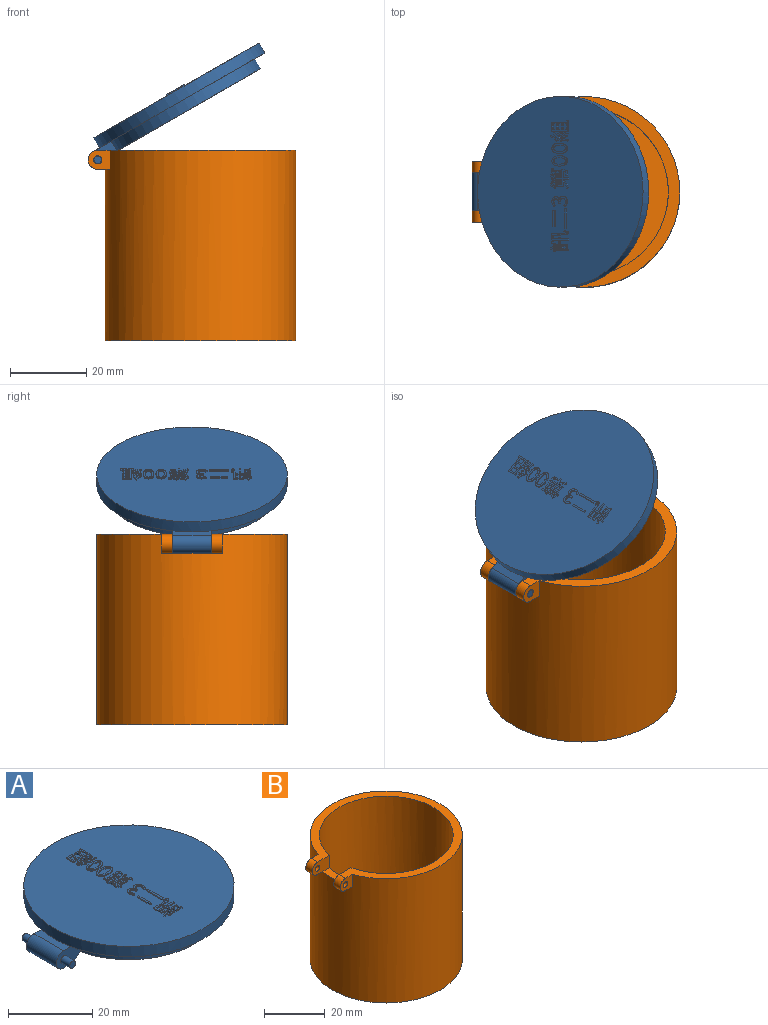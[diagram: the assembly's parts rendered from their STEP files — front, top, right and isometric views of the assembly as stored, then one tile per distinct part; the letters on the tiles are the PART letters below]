
ASSEMBLY  parts=2 mates=1
PART A: 240 faces, bbox 54.4x50x8.3 mm
  f0: plane 50x50mm, normal (0,0,1), area 1893.5mm2, adj f5,f15,f16,f17,f18,f20,f21,f22
  f1: plane 10x2.43mm, normal (0,0,1), area 20.9mm2, adj f2,f3,f5,f13
  f2: plane 8x5mm, normal (0,-1,0), area 31.8mm2, adj f1,f4,f6,f7,f9,f13,f14
  f3: plane 8x5mm, normal (0,1,0), area 31.8mm2, adj f1,f4,f6,f7,f11,f13,f14
  f4: plane 10x1.5mm, normal (0,0,-1), area 15mm2, adj f2,f3,f13,f14
  f5: cylinder r=25mm len=50mm, axis (0,0,1), area 471.2mm2, adj f0,f1,f6
  f6: plane 50x49.5mm, normal (0,0,-1), area 412.7mm2, adj f2,f3,f5,f7
  f7: cylinder r=22mm len=44mm, axis (0,0,1), area 384.4mm2, adj f2,f3,f6,f8
  f8: plane 44x43.42mm, normal (0,0,-1), area 1516.7mm2, adj f7,f14
  f9: cylinder r=1mm len=3mm, axis (0,1,0), area 18.8mm2, adj f2,f10
  f10: plane 2x2mm, normal (0,-1,0), area 3.1mm2, adj f9
  f11: cylinder r=1mm len=3mm, axis (0,-1,0), area 18.8mm2, adj f3,f12
  f12: plane 2x2mm, normal (0,1,0), area 3.1mm2, adj f11
  f13: cylinder r=2.5mm len=10mm, axis (0,-1,0), area 78.5mm2, adj f1,f2,f3,f4
  f14: cylinder r=5mm len=10mm, axis (0,1,0), area 46.4mm2, adj f2,f3,f4,f8
  f15: plane 0.33x0.3mm, normal (0.85,0.53,0), area 0.1mm2, adj f0,f16,f18,f19
  f16: extruded ~0.76x0.43mm, area 0.3mm2, adj f0,f15,f17,f19
  f17: plane 0.31x0.3mm, normal (-0.87,-0.49,0), area 0.1mm2, adj f0,f16,f18,f19
  f18: extruded ~0.79x0.42mm, area 0.3mm2, adj f0,f15,f17,f19
  f19: plane 0.97x0.74mm, normal (0,0,1), area 0.3mm2, adj f15,f16,f17,f18
  f20: plane 0.36x0.3mm, normal (0,1,0), area 0.1mm2, adj f0,f21,f23,f24
  f21: plane 2.13x0.3mm, normal (-1,0,0), area 0.6mm2, adj f0,f20,f22,f24
  f22: plane 0.36x0.3mm, normal (0,-1,0), area 0.1mm2, adj f0,f21,f23,f24
  f23: plane 2.13x0.3mm, normal (1,0,0), area 0.6mm2, adj f0,f20,f22,f24
  f24: plane 2.13x0.36mm, normal (0,0,1), area 0.8mm2, adj f20,f21,f22,f23
  f25: plane 1.67x0.3mm, normal (1,0,0), area 0.5mm2, adj f0,f26,f28,f29
  f26: plane 0.35x0.3mm, normal (0,1,0), area 0.1mm2, adj f0,f25,f27,f29
  f27: plane 1.67x0.3mm, normal (-1,0,0), area 0.5mm2, adj f0,f26,f28,f29
  f28: plane 0.35x0.3mm, normal (0,-1,0), area 0.1mm2, adj f0,f25,f27,f29
  f29: plane 1.67x0.35mm, normal (0,0,1), area 0.6mm2, adj f25,f26,f27,f28
  f30: plane 0.96x0.3mm, normal (1,0,0), area 0.3mm2, adj f31,f39,f40,f41
  f31: plane 0.98x0.3mm, normal (0,-1,0), area 0.3mm2, adj f30,f32,f40,f41
  f32: plane 0.96x0.3mm, normal (-1,0,0), area 0.3mm2, adj f31,f39,f40,f41
  f33: plane 1.71x0.3mm, normal (0,1,0), area 0.5mm2, adj f0,f34,f38,f40
  f34: plane 1.68x0.3mm, normal (-1,0,0), area 0.5mm2, adj f0,f33,f35,f40
  f35: plane 1.99x0.3mm, normal (0,-1,0), area 0.6mm2, adj f0,f34,f36,f40
  f36: plane 0.36x0.3mm, normal (1,0,0), area 0.1mm2, adj f0,f35,f37,f40
  f37: plane 0.3x0.28mm, normal (0,1,0), area 0.1mm2, adj f0,f36,f38,f40
  f38: plane 1.32x0.3mm, normal (1,0,0), area 0.4mm2, adj f0,f33,f37,f40
  f39: plane 0.98x0.3mm, normal (0,1,0), area 0.3mm2, adj f30,f32,f40,f41
  f40: plane 1.99x1.68mm, normal (0,0,1), area 2mm2, adj f30,f31,f32,f33,f34,f35,f36,f37
  f41: plane 0.98x0.96mm, normal (0,0,1), area 0.9mm2, adj f30,f31,f32,f39
  f42: plane 0.35x0.3mm, normal (0,-1,0), area 0.1mm2, adj f0,f43,f45,f46
  f43: plane 1.68x0.3mm, normal (1,0,0), area 0.5mm2, adj f0,f42,f44,f46
  f44: plane 0.35x0.3mm, normal (0,1,0), area 0.1mm2, adj f0,f43,f45,f46
  f45: plane 1.68x0.3mm, normal (-1,0,0), area 0.5mm2, adj f0,f42,f44,f46
  f46: plane 1.68x0.35mm, normal (0,0,1), area 0.6mm2, adj f42,f43,f44,f45
  f47: plane 2.58x0.3mm, normal (-1,0,0), area 0.8mm2, adj f0,f48,f66,f67
  f48: plane 0.42x0.3mm, normal (0,-1,0), area 0.1mm2, adj f0,f47,f49,f67
  f49: plane 0.74x0.3mm, normal (1,0,0), area 0.2mm2, adj f0,f48,f50,f67
  f50: plane 1.75x0.3mm, normal (0,-1,0), area 0.5mm2, adj f0,f49,f51,f67
  f51: plane 0.8x0.3mm, normal (-1,0,0), area 0.2mm2, adj f0,f50,f52,f67
  f52: plane 0.41x0.3mm, normal (0,-1,0), area 0.1mm2, adj f0,f51,f53,f67
  f53: plane 0.8x0.3mm, normal (1,0,0), area 0.2mm2, adj f0,f52,f54,f67
  f54: plane 2.5x0.3mm, normal (0,-1,0), area 0.7mm2, adj f0,f53,f55,f67
  f55: plane 0.42x0.3mm, normal (1,0,0), area 0.1mm2, adj f0,f54,f56,f67
  f56: plane 2.5x0.3mm, normal (0,1,0), area 0.7mm2, adj f0,f55,f57,f67
  f57: plane 0.78x0.3mm, normal (1,0,0), area 0.2mm2, adj f0,f56,f58,f67
  f58: plane 0.41x0.3mm, normal (0,1,0), area 0.1mm2, adj f0,f57,f59,f67
  f59: plane 0.78x0.3mm, normal (-1,0,0), area 0.2mm2, adj f0,f58,f60,f67
  f60: plane 1.75x0.3mm, normal (0,1,0), area 0.5mm2, adj f0,f59,f61,f67
  f61: plane 0.98x0.3mm, normal (1,0,0), area 0.3mm2, adj f0,f60,f62,f67
  f62: extruded ~4.55x0.56mm, area 1.4mm2, adj f0,f61,f63,f67
  f63: extruded ~0.94x0.53mm, area 0.4mm2, adj f0,f62,f64,f67
  f64: extruded ~0.32x0.3mm, area 0.1mm2, adj f0,f63,f65,f67
  f65: extruded ~0.8x0.3mm, area 0.2mm2, adj f0,f64,f66,f67
  f66: extruded ~4.54x0.3mm, area 1.4mm2, adj f0,f47,f65,f67
  f67: plane 5.08x3.29mm, normal (0,0,1), area 5.9mm2, adj f47,f48,f49,f50,f51,f52,f53,f54
  f68: plane 4.23x0.3mm, normal (-1,0,0), area 1.3mm2, adj f0,f69,f71,f72
  f69: plane 0.47x0.3mm, normal (0,-1,0), area 0.1mm2, adj f0,f68,f70,f72
  f70: plane 4.23x0.3mm, normal (1,0,0), area 1.3mm2, adj f0,f69,f71,f72
  f71: plane 0.47x0.3mm, normal (0,1,0), area 0.1mm2, adj f0,f68,f70,f72
  f72: plane 4.23x0.47mm, normal (0,0,1), area 2mm2, adj f68,f69,f70,f71
  f73: plane 5.23x0.3mm, normal (-1,0,0), area 1.6mm2, adj f0,f74,f76,f77
  f74: plane 0.48x0.3mm, normal (0,-1,0), area 0.1mm2, adj f0,f73,f75,f77
  f75: plane 5.23x0.3mm, normal (1,0,0), area 1.6mm2, adj f0,f74,f76,f77
  f76: plane 0.48x0.3mm, normal (0,1,0), area 0.1mm2, adj f0,f73,f75,f77
  f77: plane 5.23x0.48mm, normal (0,0,1), area 2.5mm2, adj f73,f74,f75,f76
  f78: extruded ~1.39x0.59mm, area 0.5mm2, adj f0,f79,f93,f94
  f79: extruded ~1.39x1.24mm, area 0.6mm2, adj f0,f78,f80,f94
  f80: extruded ~1.1x0.93mm, area 0.5mm2, adj f0,f79,f81,f94
  f81: plane 0.3x0.02mm, normal (0,1,0), area 0mm2, adj f0,f80,f82,f94
  f82: extruded ~1.05x0.78mm, area 0.4mm2, adj f0,f81,f83,f94
  f83: extruded ~1.26x1.09mm, area 0.6mm2, adj f0,f82,f84,f94
  f84: extruded ~1.22x0.52mm, area 0.4mm2, adj f0,f83,f85,f94
  f85: plane 0.35x0.3mm, normal (0.65,-0.76,0), area 0.1mm2, adj f0,f84,f86,f94
  f86: extruded ~0.9x0.43mm, area 0.3mm2, adj f0,f85,f87,f94
  f87: extruded ~0.74x0.7mm, area 0.3mm2, adj f0,f86,f88,f94
  f88: extruded ~1.2x0.83mm, area 0.5mm2, adj f0,f87,f89,f94
  f89: plane 0.42x0.3mm, normal (0,-1,0), area 0.1mm2, adj f0,f88,f90,f94
  f90: extruded ~1.35x0.87mm, area 0.5mm2, adj f0,f89,f91,f94
  f91: extruded ~0.88x0.81mm, area 0.4mm2, adj f0,f90,f92,f94
  f92: extruded ~1.08x0.5mm, area 0.4mm2, adj f0,f91,f93,f94
  f93: plane 0.36x0.3mm, normal (-0.61,-0.79,0), area 0.1mm2, adj f0,f78,f92,f94
  f94: plane 4.51x2.79mm, normal (0,0,1), area 4.4mm2, adj f78,f79,f80,f81,f82,f83,f84,f85
  f95: plane 0.51x0.3mm, normal (1,0,0), area 0.2mm2, adj f0,f96,f107,f108
  f96: plane 0.3x0.23mm, normal (-0.8,-0.61,0), area 0.1mm2, adj f0,f95,f97,f108
  f97: extruded ~0.6x0.56mm, area 0.2mm2, adj f0,f96,f98,f108
  f98: plane 0.3x0.29mm, normal (0.77,0.64,0), area 0.1mm2, adj f0,f97,f99,f108
  f99: extruded ~0.53x0.53mm, area 0.2mm2, adj f0,f98,f100,f108
  f100: plane 1.12x0.3mm, normal (1,0,0), area 0.3mm2, adj f0,f99,f101,f108
  f101: plane 0.36x0.3mm, normal (0,1,0), area 0.1mm2, adj f0,f100,f102,f108
  f102: plane 1.52x0.3mm, normal (-1,0,0), area 0.5mm2, adj f0,f101,f103,f108
  f103: extruded ~0.36x0.3mm, area 0.1mm2, adj f0,f102,f104,f108
  f104: plane 0.39x0.3mm, normal (-0.96,0.27,0), area 0.1mm2, adj f0,f103,f105,f108
  f105: extruded ~1.29x0.9mm, area 0.5mm2, adj f0,f104,f106,f108
  f106: extruded ~0.31x0.3mm, area 0.1mm2, adj f0,f105,f107,f108
  f107: extruded ~0.77x0.61mm, area 0.3mm2, adj f0,f95,f106,f108
  f108: plane 2.64x1.6mm, normal (0,0,1), area 1.5mm2, adj f95,f96,f97,f98,f99,f100,f101,f102
  f109: plane 1.33x0.3mm, normal (1,0,0), area 0.4mm2, adj f110,f142,f143,f145
  f110: plane 0.55x0.3mm, normal (0,-1,0), area 0.2mm2, adj f109,f111,f143,f145
  f111: plane 1.42x0.3mm, normal (-1,0,0), area 0.4mm2, adj f110,f142,f143,f145
  f112: plane 0.55x0.3mm, normal (0,1,0), area 0.2mm2, adj f113,f140,f143,f144
  f113: plane 1.55x0.3mm, normal (1,0,0), area 0.5mm2, adj f112,f114,f143,f144
  f114: plane 0.55x0.3mm, normal (0,-1,0), area 0.2mm2, adj f113,f140,f143,f144
  f115: plane 2.18x0.3mm, normal (-1,0,0), area 0.7mm2, adj f0,f116,f141,f143
  f116: plane 0.55x0.3mm, normal (0,1,0), area 0.2mm2, adj f0,f115,f117,f143
  f117: plane 1.99x0.3mm, normal (1,0,0), area 0.6mm2, adj f0,f116,f118,f143
  f118: plane 1.29x0.3mm, normal (0,1,0), area 0.4mm2, adj f0,f117,f119,f143
  f119: plane 4.34x0.3mm, normal (-1,0,0), area 1.3mm2, adj f0,f118,f120,f143
  f120: plane 0.37x0.3mm, normal (0,-1,0), area 0.1mm2, adj f0,f119,f121,f143
  f121: plane 1.92x0.3mm, normal (1,0,0), area 0.6mm2, adj f0,f120,f122,f143
  f122: plane 0.55x0.3mm, normal (0,-1,0), area 0.2mm2, adj f0,f121,f123,f143
  f123: plane 1.71x0.3mm, normal (-1,0,0), area 0.5mm2, adj f0,f122,f124,f143
  f124: extruded ~1.31x0.3mm, area 0.4mm2, adj f0,f123,f125,f143
  f125: plane 1.57x0.3mm, normal (1,0,0), area 0.5mm2, adj f0,f124,f126,f143
  f126: extruded ~1.93x1.19mm, area 0.7mm2, adj f0,f125,f127,f143
  f127: extruded ~0.35x0.3mm, area 0.1mm2, adj f0,f126,f128,f143
  f128: extruded ~1.99x1.37mm, area 0.7mm2, adj f0,f127,f129,f143
  f129: plane 1.36x0.3mm, normal (0,-1,0), area 0.4mm2, adj f0,f128,f130,f143
  f130: plane 0.43x0.3mm, normal (1,0,0), area 0.1mm2, adj f0,f129,f131,f143
  f131: plane 1.53x0.3mm, normal (0,1,0), area 0.5mm2, adj f0,f130,f132,f143
  f132: plane 1.71x0.3mm, normal (1,0,0), area 0.5mm2, adj f0,f131,f133,f143
  f133: extruded ~0.85x0.3mm, area 0.3mm2, adj f0,f132,f134,f143
  f134: extruded ~0.3x0.21mm, area 0.1mm2, adj f0,f133,f135,f143
  f135: extruded ~0.67x0.3mm, area 0.2mm2, adj f0,f134,f136,f143
  f136: extruded ~0.41x0.3mm, area 0.1mm2, adj f0,f135,f137,f143
  f137: extruded ~0.75x0.3mm, area 0.2mm2, adj f0,f136,f138,f143
  f138: extruded ~0.37x0.3mm, area 0.1mm2, adj f0,f137,f139,f143
  f139: extruded ~1.32x0.31mm, area 0.4mm2, adj f0,f138,f141,f143
  f140: plane 1.55x0.3mm, normal (-1,0,0), area 0.5mm2, adj f112,f114,f143,f144
  f141: extruded ~0.3x0.18mm, area 0.1mm2, adj f0,f115,f139,f143
  f142: extruded ~0.55x0.3mm, area 0.2mm2, adj f109,f111,f143,f145
  f143: plane 4.89x3.76mm, normal (0,0,1), area 8.3mm2, adj f109,f110,f111,f112,f113,f114,f115,f116
  f144: plane 1.55x0.55mm, normal (0,0,1), area 0.8mm2, adj f112,f113,f114,f140
  f145: plane 1.42x0.55mm, normal (0,0,1), area 0.8mm2, adj f109,f110,f111,f142
  f146: plane 1.79x0.3mm, normal (-1,0,0), area 0.5mm2, adj f0,f147,f158,f159
  f147: extruded ~0.37x0.3mm, area 0.1mm2, adj f0,f146,f148,f159
  f148: plane 0.41x0.3mm, normal (-0.97,0.23,0), area 0.1mm2, adj f0,f147,f149,f159
  f149: extruded ~1.1x0.74mm, area 0.4mm2, adj f0,f148,f150,f159
  f150: extruded ~0.33x0.3mm, area 0.1mm2, adj f0,f149,f151,f159
  f151: extruded ~0.55x0.45mm, area 0.2mm2, adj f0,f150,f152,f159
  f152: plane 0.66x0.3mm, normal (1,0,0), area 0.2mm2, adj f0,f151,f153,f159
  f153: plane 0.3x0.26mm, normal (-0.78,-0.63,0), area 0.1mm2, adj f0,f152,f154,f159
  f154: extruded ~0.61x0.58mm, area 0.3mm2, adj f0,f153,f155,f159
  f155: plane 0.3x0.29mm, normal (0.76,0.65,0), area 0.1mm2, adj f0,f154,f156,f159
  f156: extruded ~0.59x0.53mm, area 0.2mm2, adj f0,f155,f157,f159
  f157: plane 1.28x0.3mm, normal (1,0,0), area 0.4mm2, adj f0,f156,f158,f159
  f158: plane 0.35x0.3mm, normal (0,1,0), area 0.1mm2, adj f0,f146,f157,f159
  f159: plane 2.78x1.6mm, normal (0,0,1), area 1.6mm2, adj f146,f147,f148,f149,f150,f151,f152,f153
  f160: extruded ~2.27x1.36mm, area 0.9mm2, adj f0,f161,f167,f168
  f161: extruded ~2.27x1.35mm, area 0.9mm2, adj f0,f160,f162,f168
  f162: extruded ~2.24x1.35mm, area 0.9mm2, adj f0,f161,f167,f168
  f163: extruded ~1.83x0.83mm, area 0.7mm2, adj f164,f166,f168,f169
  f164: extruded ~1.83x0.83mm, area 0.7mm2, adj f163,f165,f168,f169
  f165: extruded ~1.8x0.83mm, area 0.7mm2, adj f164,f166,f168,f169
  f166: extruded ~1.8x0.83mm, area 0.7mm2, adj f163,f165,f168,f169
  f167: extruded ~2.24x1.36mm, area 0.9mm2, adj f0,f160,f162,f168
  f168: plane 4.51x2.71mm, normal (0,0,1), area 5.1mm2, adj f160,f161,f162,f163,f164,f165,f166,f167
  f169: plane 3.64x1.66mm, normal (0,0,1), area 5mm2, adj f163,f164,f165,f166
  f170: extruded ~2.27x1.36mm, area 0.9mm2, adj f0,f171,f177,f178
  f171: extruded ~2.27x1.35mm, area 0.9mm2, adj f0,f170,f172,f178
  f172: extruded ~2.24x1.35mm, area 0.9mm2, adj f0,f171,f177,f178
  f173: extruded ~1.83x0.83mm, area 0.7mm2, adj f174,f176,f178,f179
  f174: extruded ~1.83x0.83mm, area 0.7mm2, adj f173,f175,f178,f179
  f175: extruded ~1.8x0.83mm, area 0.7mm2, adj f174,f176,f178,f179
  f176: extruded ~1.8x0.83mm, area 0.7mm2, adj f173,f175,f178,f179
  f177: extruded ~2.24x1.36mm, area 0.9mm2, adj f0,f170,f172,f178
  f178: plane 4.51x2.71mm, normal (0,0,1), area 5.1mm2, adj f170,f171,f172,f173,f174,f175,f176,f177
  f179: plane 3.64x1.66mm, normal (0,0,1), area 5mm2, adj f173,f174,f175,f176
  f180: plane 0.37x0.3mm, normal (0.95,0.31,0), area 0.1mm2, adj f0,f181,f199,f200
  f181: extruded ~1.23x0.4mm, area 0.4mm2, adj f0,f180,f182,f200
  f182: plane 0.34x0.3mm, normal (-0.96,-0.28,0), area 0.1mm2, adj f0,f181,f183,f200
  f183: extruded ~0.55x0.3mm, area 0.2mm2, adj f0,f182,f184,f200
  f184: plane 1.05x0.3mm, normal (-0.99,-0.13,0), area 0.3mm2, adj f0,f183,f185,f200
  f185: extruded ~1.89x1.41mm, area 0.7mm2, adj f0,f184,f186,f200
  f186: plane 0.38x0.3mm, normal (-0.85,0.52,0), area 0.1mm2, adj f0,f185,f187,f200
  f187: extruded ~0.78x0.46mm, area 0.3mm2, adj f0,f186,f188,f200
  f188: plane 0.69x0.3mm, normal (-1,-0.09,0), area 0.2mm2, adj f0,f187,f189,f200
  f189: extruded ~1.58x0.97mm, area 0.6mm2, adj f0,f188,f190,f200
  f190: plane 0.4x0.3mm, normal (-0.92,0.39,0), area 0.1mm2, adj f0,f189,f191,f200
  f191: extruded ~1.5x0.83mm, area 0.5mm2, adj f0,f190,f192,f200
  f192: extruded ~0.34x0.33mm, area 0.1mm2, adj f0,f191,f193,f200
  f193: extruded ~0.4x0.3mm, area 0.1mm2, adj f0,f192,f194,f200
  f194: extruded ~0.9x0.3mm, area 0.3mm2, adj f0,f193,f195,f200
  f195: extruded ~0.68x0.54mm, area 0.3mm2, adj f0,f194,f196,f200
  f196: extruded ~0.45x0.39mm, area 0.2mm2, adj f0,f195,f197,f200
  f197: extruded ~0.42x0.3mm, area 0.1mm2, adj f0,f196,f198,f200
  f198: extruded ~1.71x0.32mm, area 0.5mm2, adj f0,f197,f199,f200
  f199: extruded ~0.36x0.3mm, area 0.1mm2, adj f0,f180,f198,f200
  f200: plane 3.59x2.33mm, normal (0,0,1), area 3.4mm2, adj f180,f181,f182,f183,f184,f185,f186,f187
  f201: plane 0.37x0.3mm, normal (-0.99,0.16,0), area 0.1mm2, adj f0,f202,f204,f205
  f202: extruded ~1.36x0.3mm, area 0.4mm2, adj f0,f201,f203,f205
  f203: extruded ~0.36x0.3mm, area 0.1mm2, adj f0,f202,f204,f205
  f204: extruded ~1.44x0.3mm, area 0.4mm2, adj f0,f201,f203,f205
  f205: plane 1.5x0.66mm, normal (0,0,1), area 0.5mm2, adj f201,f202,f203,f204
  f206: plane 0.35x0.3mm, normal (-0.98,-0.18,0), area 0.1mm2, adj f0,f207,f209,f210
  f207: extruded ~1.28x0.3mm, area 0.4mm2, adj f0,f206,f208,f210
  f208: plane 0.37x0.3mm, normal (0.98,0.19,0), area 0.1mm2, adj f0,f207,f209,f210
  f209: extruded ~1.27x0.3mm, area 0.4mm2, adj f0,f206,f208,f210
  f210: plane 1.34x0.52mm, normal (0,0,1), area 0.5mm2, adj f206,f207,f208,f209
  f211: plane 0.33x0.3mm, normal (-0.95,-0.31,0), area 0.1mm2, adj f0,f212,f214,f215
  f212: extruded ~1.02x0.3mm, area 0.3mm2, adj f0,f211,f213,f215
  f213: plane 0.35x0.3mm, normal (0.95,0.32,0), area 0.1mm2, adj f0,f212,f214,f215
  f214: extruded ~1.01x0.31mm, area 0.3mm2, adj f0,f211,f213,f215
  f215: plane 1.13x0.64mm, normal (0,0,1), area 0.4mm2, adj f211,f212,f213,f214
  f216: plane 1.16x0.3mm, normal (0,1,0), area 0.3mm2, adj f217,f235,f236,f239
  f217: plane 1.53x0.3mm, normal (1,0,0), area 0.5mm2, adj f216,f218,f236,f239
  f218: plane 1.16x0.3mm, normal (0,-1,0), area 0.3mm2, adj f217,f235,f236,f239
  f219: plane 1.53x0.3mm, normal (1,0,0), area 0.5mm2, adj f220,f232,f236,f238
  f220: plane 1.1x0.3mm, normal (0,-1,0), area 0.3mm2, adj f219,f221,f236,f238
  f221: plane 1.53x0.3mm, normal (-1,0,0), area 0.5mm2, adj f220,f232,f236,f238
  f222: plane 1.13x0.3mm, normal (0,-1,0), area 0.3mm2, adj f223,f233,f236,f237
  f223: plane 1.53x0.3mm, normal (-1,0,0), area 0.5mm2, adj f222,f224,f236,f237
  f224: plane 1.13x0.3mm, normal (0,1,0), area 0.3mm2, adj f223,f233,f236,f237
  f225: plane 0.4x0.3mm, normal (-1,0,0), area 0.1mm2, adj f0,f226,f234,f236
  f226: plane 4.59x0.3mm, normal (0,1,0), area 1.4mm2, adj f0,f225,f227,f236
  f227: plane 2.36x0.3mm, normal (-1,0,0), area 0.7mm2, adj f0,f226,f228,f236
  f228: plane 4.59x0.3mm, normal (0,-1,0), area 1.4mm2, adj f0,f227,f229,f236
  f229: plane 0.52x0.3mm, normal (-1,0,0), area 0.2mm2, adj f0,f228,f230,f236
  f230: plane 0.4x0.3mm, normal (0,-1,0), area 0.1mm2, adj f0,f229,f231,f236
  f231: plane 3.28x0.3mm, normal (1,0,0), area 1mm2, adj f0,f230,f234,f236
  f232: plane 1.1x0.3mm, normal (0,1,0), area 0.3mm2, adj f219,f221,f236,f238
  f233: plane 1.53x0.3mm, normal (1,0,0), area 0.5mm2, adj f222,f224,f236,f237
  f234: plane 0.4x0.3mm, normal (0,1,0), area 0.1mm2, adj f0,f225,f231,f236
  f235: plane 1.53x0.3mm, normal (-1,0,0), area 0.5mm2, adj f216,f218,f236,f239
  f236: plane 4.99x3.28mm, normal (0,0,1), area 7mm2, adj f216,f217,f218,f219,f220,f221,f222,f223
  f237: plane 1.53x1.13mm, normal (0,0,1), area 1.7mm2, adj f222,f223,f224,f233
  f238: plane 1.53x1.1mm, normal (0,0,1), area 1.7mm2, adj f219,f220,f221,f232
  f239: plane 1.53x1.16mm, normal (0,0,1), area 1.8mm2, adj f216,f217,f218,f235
PART B: 16 faces, bbox 54.4x50x50 mm
  f0: plane 51.92x50mm, normal (0,0,1), area 429.5mm2, adj f1,f2,f3,f6,f7,f11,f14,f15
  f1: plane 8x5mm, normal (0,-1,0), area 33.9mm2, adj f0,f4,f7,f10,f13,f15
  f2: plane 8x5mm, normal (0,1,0), area 33.9mm2, adj f0,f5,f7,f10,f12,f14
  f3: plane 5.74x5mm, normal (0,1,0), area 22.5mm2, adj f0,f4,f6,f13,f15
  f4: plane 3.24x3mm, normal (0,0,-1), area 8.4mm2, adj f1,f3,f6,f15
  f5: plane 3.24x3mm, normal (0,0,-1), area 8.4mm2, adj f2,f6,f11,f14
  f6: cylinder r=25mm len=50mm, axis (0,0,-1), area 7772.5mm2, adj f0,f3,f4,f5,f8,f10,f11
  f7: cylinder r=22mm len=47mm, axis (0,0,-1), area 6446.4mm2, adj f0,f1,f2,f9,f10
  f8: plane 50x50mm, normal (0,0,-1), area 1963.5mm2, adj f6
  f9: plane 44x44mm, normal (0,0,1), area 1520.5mm2, adj f7
  f10: plane 10x3.58mm, normal (0,0,1), area 30.2mm2, adj f1,f2,f6,f7
  f11: plane 5.74x5mm, normal (0,-1,0), area 22.5mm2, adj f0,f5,f6,f12,f14
  f12: cylinder r=1.05mm len=3mm, axis (0,-1,0), area 19.8mm2, adj f2,f11
  f13: cylinder r=1.05mm len=3mm, axis (0,-1,0), area 19.8mm2, adj f1,f3
  f14: cylinder r=2.5mm len=5mm, axis (0,-1,0), area 23.6mm2, adj f0,f2,f5,f11
  f15: cylinder r=2.5mm len=5mm, axis (0,-1,0), area 23.6mm2, adj f0,f1,f3,f4
PLACE A rot(axis=(0,-1,0),29.9deg) t=(-5.34,4.59,50.32)mm
PLACE B t=(0.97,4.59,-15.35)mm fixed
MATE revolute A.f9 <-> B.f12  axis (0,-1,0) through (-25.95,-3.41,32.15)mm
